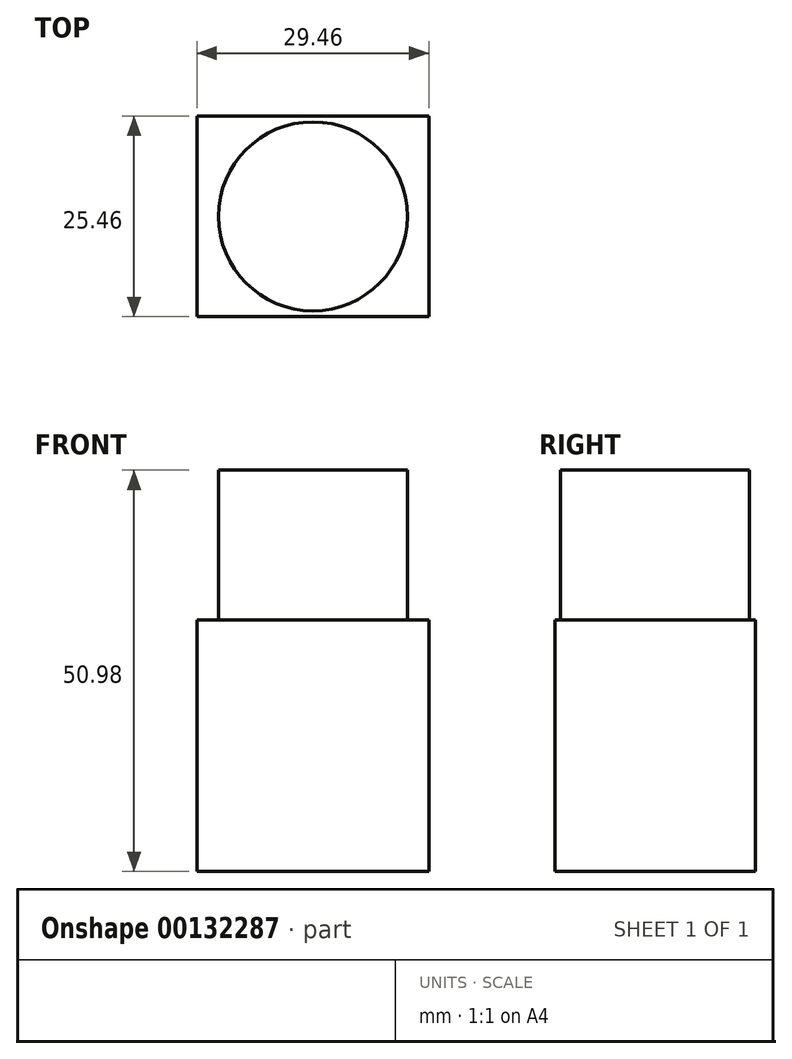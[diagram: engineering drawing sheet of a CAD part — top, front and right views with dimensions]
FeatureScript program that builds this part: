
annotation { "Feature Type Name" : "Feature", "Feature Type Description" : "" }
export const myFeature = defineFeature(function(context is Context, id is Id, definition is map)
    precondition{}
    {
        {
            var Q0;
            Q0=qCreatedBy(makeId("Top.planeOp"),FACE);
            var sketch = newSketch(context, id + "F0", { "sketchPlane" : qUnion([Q0])});
            skLineSegment(sketch, "E0.bottom", {"start": v(14.73, -12.73) * mm, "end": v(-14.73, -12.73) * mm});
            skLineSegment(sketch, "E0.top", {"start": v(14.73, 12.73) * mm, "end": v(-14.73, 12.73) * mm});
            skLineSegment(sketch, "E0.left", {"start": v(14.73, -12.73) * mm, "end": v(14.73, 12.73) * mm});
            skLineSegment(sketch, "E0.right", {"start": v(-14.73, -12.73) * mm, "end": v(-14.73, 12.73) * mm});
            skPoint(sketch, "E0.middle", {"position": v(0, 0) * mm});
            skSolve(sketch);
        }
        {
            var Q0;
            Q0 = qSketchRegion(id + "F0", true);
            extrude(context, id + "F1", {"entities" : qUnion([Q0]), "depth" : 50.98 * mm});
        }
        {
            var Q0;
            Q0=makeQuery(id+"F1.opExtrude","CAP_FACE",FACE,{"disambiguationData":[OSD([sQuery(id+"F0.wireOp",EDGE,"E0.bottom"),sQuery(id+"F0.wireOp",EDGE,"E0.top"),sQuery(id+"F0.wireOp",EDGE,"E0.left"),sQuery(id+"F0.wireOp",EDGE,"E0.right")])],"isStart":false});
            var sketch = newSketch(context, id + "F2", { "sketchPlane" : qUnion([Q0])});
            skCircle(sketch, "E1", {"center": v(0, 0) * mm, "radius": 12 * mm});
            skLineSegment(sketch, "E2.bottom", {"start": v(19.95, -18.3) * mm, "end": v(-19.95, -18.3) * mm});
            skLineSegment(sketch, "E2.top", {"start": v(19.95, 18.3) * mm, "end": v(-19.95, 18.3) * mm});
            skLineSegment(sketch, "E2.left", {"start": v(19.95, -18.3) * mm, "end": v(19.95, 18.3) * mm});
            skLineSegment(sketch, "E2.right", {"start": v(-19.95, -18.3) * mm, "end": v(-19.95, 18.3) * mm});
            skSolve(sketch);
        }
        {
            var Q0;
            Q0 = qSketchRegion(id + "F2", true);
            extrude(context, id + "F3", {"entities" : qUnion([Q0]), "operationType" : NewBodyOperationType.REMOVE, "oppositeDirection" : true, "depth" : 19.05 * mm});
        }
    });
